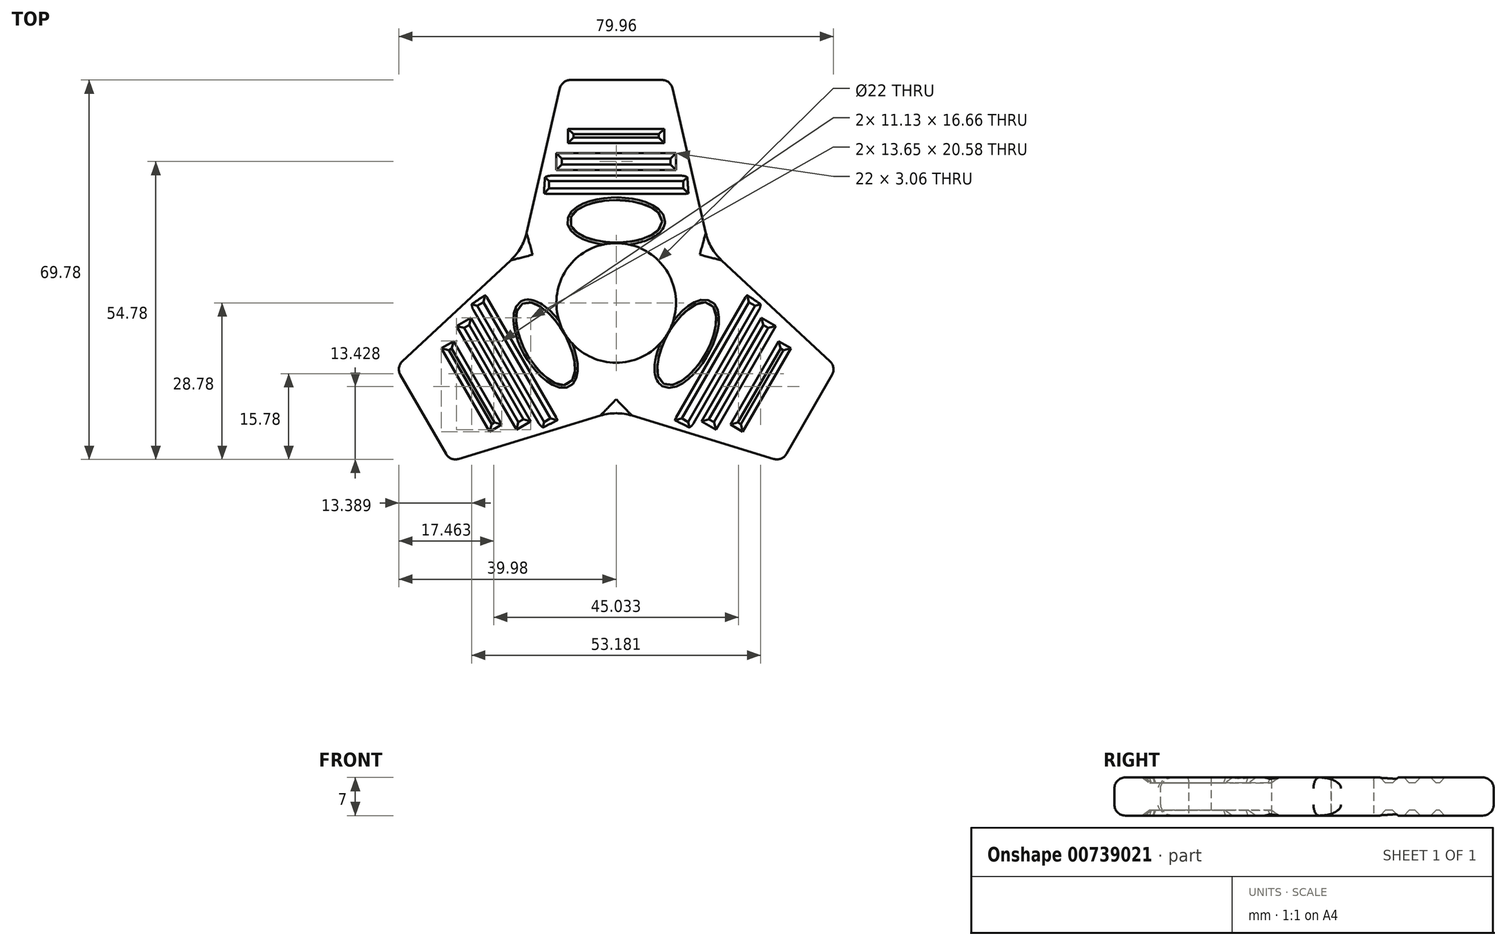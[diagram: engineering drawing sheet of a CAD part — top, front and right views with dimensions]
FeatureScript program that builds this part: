
annotation { "Feature Type Name" : "Feature", "Feature Type Description" : "" }
export const myFeature = defineFeature(function(context is Context, id is Id, definition is map)
    precondition{}
    {
        {
            var Q0;
            Q0=qCreatedBy(makeId("Top.planeOp"),FACE);
            var sketch = newSketch(context, id + "F0", { "sketchPlane" : qUnion([Q0])});
            skCircle(sketch, "E0", {"center": v(0, 0) * mm, "radius": 11 * mm});
            skLineSegment(sketch, "E1", {"start": v(0, 11) * mm, "end": v(0, 41) * mm});
            skLineSegment(sketch, "E2", {"start": v(0, 41) * mm, "end": v(10, 41) * mm});
            skLineSegment(sketch, "E3", {"start": v(0, 41) * mm, "end": v(-10, 41) * mm});
            skLineSegment(sketch, "E4", {"start": v(-10, 41) * mm, "end": v(-19.47, 0) * mm});
            skLineSegment(sketch, "E5", {"start": v(10, 41) * mm, "end": v(19.47, 0) * mm});
            skLineSegment(sketch, "E6", {"start": v(-19.47, 0) * mm, "end": v(-11, 0) * mm});
            skLineSegment(sketch, "E7", {"start": v(19.47, 0) * mm, "end": v(11, 0) * mm});
            skLineSegment(sketch, "E8.bottom", {"start": v(8.86, 32.01) * mm, "end": v(-8.86, 32.01) * mm});
            skLineSegment(sketch, "E8.top", {"start": v(8.86, 29.4) * mm, "end": v(-8.86, 29.4) * mm});
            skLineSegment(sketch, "E8.left", {"start": v(8.86, 32.01) * mm, "end": v(8.86, 29.4) * mm});
            skLineSegment(sketch, "E8.right", {"start": v(-8.86, 32.01) * mm, "end": v(-8.86, 29.4) * mm});
            skPoint(sketch, "E8.middle", {"position": v(0, 30.7) * mm});
            skLineSegment(sketch, "E9.bottom", {"start": v(11, 27.53) * mm, "end": v(-11, 27.53) * mm});
            skLineSegment(sketch, "E9.top", {"start": v(11, 24.47) * mm, "end": v(-11, 24.47) * mm});
            skLineSegment(sketch, "E9.left", {"start": v(11, 27.53) * mm, "end": v(11, 24.47) * mm});
            skLineSegment(sketch, "E9.right", {"start": v(-11, 27.53) * mm, "end": v(-11, 24.47) * mm});
            skPoint(sketch, "E9.middle", {"position": v(0, 26) * mm});
            skLineSegment(sketch, "E10.bottom", {"start": v(13.34, 23.4) * mm, "end": v(-13.34, 23.4) * mm});
            skLineSegment(sketch, "E10.top", {"start": v(13.34, 20.09) * mm, "end": v(-13.34, 20.09) * mm});
            skLineSegment(sketch, "E10.left", {"start": v(13.34, 23.4) * mm, "end": v(13.34, 20.09) * mm});
            skLineSegment(sketch, "E10.right", {"start": v(-13.34, 23.4) * mm, "end": v(-13.34, 20.09) * mm});
            skPoint(sketch, "E10.middle", {"position": v(0, 21.74) * mm});
            skSolve(sketch);
        }
        {
            var Q0;
            {var subQ0=sQuery(id+"F0.wireOp",EDGE,"E1");Q0=makeQuery(id+"F0.imprint","IMPRINT",FACE,{"disambiguationData":[TD([[makeQuery(id+"F0.imprint","IMPRINT",EDGE,{"derivedFrom":subQ0}),-1.0]])]});}
            var Q1;
            {var subQ0=sQuery(id+"F0.wireOp",EDGE,"E1");Q1=makeQuery(id+"F0.imprint","IMPRINT",FACE,{"disambiguationData":[TD([[makeQuery(id+"F0.imprint","IMPRINT",EDGE,{"derivedFrom":subQ0}),1.0]])]});}
            extrude(context, id + "F1", {"entities" : qUnion([Q0, Q1]), "endBound" : BoundingType.SYMMETRIC, "depth" : 7 * mm, "offsetDistance" : 25 * mm});
        }
        {
            var Q0;
            {var subQ5=sQuery(id+"F0.wireOp",EDGE,"E8.right");Q0=makeQuery(id+"F0.imprint","IMPRINT",FACE,{"disambiguationData":[TD([[makeQuery(id+"F0.imprint","IMPRINT",EDGE,{"derivedFrom":subQ5}),1.0]])]});}
            var Q1;
            {var subQ5=sQuery(id+"F0.wireOp",EDGE,"E8.left");Q1=makeQuery(id+"F0.imprint","IMPRINT",FACE,{"disambiguationData":[TD([[makeQuery(id+"F0.imprint","IMPRINT",EDGE,{"derivedFrom":subQ5}),-1.0]])]});}
            var Q2;
            {var subQ5=sQuery(id+"F0.wireOp",EDGE,"E9.left");Q2=makeQuery(id+"F0.imprint","IMPRINT",FACE,{"disambiguationData":[TD([[makeQuery(id+"F0.imprint","IMPRINT",EDGE,{"derivedFrom":subQ5}),-1.0]])]});}
            var Q3;
            {var subQ5=sQuery(id+"F0.wireOp",EDGE,"E9.right");Q3=makeQuery(id+"F0.imprint","IMPRINT",FACE,{"disambiguationData":[TD([[makeQuery(id+"F0.imprint","IMPRINT",EDGE,{"derivedFrom":subQ5}),1.0]])]});}
            var Q4;
            {var subQ5=sQuery(id+"F0.wireOp",EDGE,"E10.right");Q4=makeQuery(id+"F0.imprint","IMPRINT",FACE,{"disambiguationData":[TD([[makeQuery(id+"F0.imprint","IMPRINT",EDGE,{"derivedFrom":subQ5}),1.0]])]});}
            var Q5;
            {var subQ5=sQuery(id+"F0.wireOp",EDGE,"E10.left");Q5=makeQuery(id+"F0.imprint","IMPRINT",FACE,{"disambiguationData":[TD([[makeQuery(id+"F0.imprint","IMPRINT",EDGE,{"derivedFrom":subQ5}),-1.0]])]});}
            extrude(context, id + "F2", {"entities" : qUnion([Q0, Q1, Q2, Q3, Q4, Q5]), "operationType" : NewBodyOperationType.ADD, "endBound" : BoundingType.SYMMETRIC, "depth" : 5 * mm, "offsetDistance" : 25 * mm});
        }
        {
            var Q0;
            Q0=makeQuery(id+"F2.opExtrude","CAP_EDGE",EDGE,{"disambiguationData":[OSD([sQuery(id+"F0.wireOp",EDGE,"E8.bottom")])],"isStart":false});
            var Q1;
            Q1=makeQuery(id+"F2.opExtrude","CAP_EDGE",EDGE,{"disambiguationData":[OSD([sQuery(id+"F0.wireOp",EDGE,"E8.left")])],"isStart":false});
            var Q2;
            Q2=makeQuery(id+"F2.opExtrude","CAP_FACE",FACE,{"disambiguationData":[OSD([sQuery(id+"F0.wireOp",EDGE,"E8.bottom"),sQuery(id+"F0.wireOp",EDGE,"E8.top"),sQuery(id+"F0.wireOp",EDGE,"E8.left"),sQuery(id+"F0.wireOp",EDGE,"E8.right")])],"isStart":false});
            var Q3;
            Q3=makeQuery(id+"F2.opExtrude","CAP_FACE",FACE,{"disambiguationData":[OSD([sQuery(id+"F0.wireOp",EDGE,"E9.bottom"),sQuery(id+"F0.wireOp",EDGE,"E9.top"),sQuery(id+"F0.wireOp",EDGE,"E9.left"),sQuery(id+"F0.wireOp",EDGE,"E9.right")])],"isStart":false});
            var Q4;
            Q4=makeQuery(id+"F2.opExtrude","CAP_FACE",FACE,{"disambiguationData":[OSD([sQuery(id+"F0.wireOp",EDGE,"E10.bottom"),sQuery(id+"F0.wireOp",EDGE,"E10.top"),sQuery(id+"F0.wireOp",EDGE,"E10.left"),sQuery(id+"F0.wireOp",EDGE,"E10.right")])],"isStart":false});
            chamfer(context, id + "F3", {"entities" : qUnion([Q0, Q1, Q2, Q3, Q4]), "chamferType" : ChamferType.OFFSET_ANGLE, "width" : 1 * mm, "oppositeDirection" : false, "angle" : 45 * degree, "tangentPropagation" : true});
        }
        {
            var Q0;
            Q0=makeQuery(id+"F2.opExtrude","CAP_FACE",FACE,{"disambiguationData":[OSD([sQuery(id+"F0.wireOp",EDGE,"E8.bottom"),sQuery(id+"F0.wireOp",EDGE,"E8.top"),sQuery(id+"F0.wireOp",EDGE,"E8.left"),sQuery(id+"F0.wireOp",EDGE,"E8.right")])],"isStart":true});
            var Q1;
            Q1=makeQuery(id+"F2.opExtrude","CAP_FACE",FACE,{"disambiguationData":[OSD([sQuery(id+"F0.wireOp",EDGE,"E9.bottom"),sQuery(id+"F0.wireOp",EDGE,"E9.top"),sQuery(id+"F0.wireOp",EDGE,"E9.left"),sQuery(id+"F0.wireOp",EDGE,"E9.right")])],"isStart":true});
            var Q2;
            Q2=makeQuery(id+"F2.opExtrude","CAP_FACE",FACE,{"disambiguationData":[OSD([sQuery(id+"F0.wireOp",EDGE,"E10.bottom"),sQuery(id+"F0.wireOp",EDGE,"E10.top"),sQuery(id+"F0.wireOp",EDGE,"E10.left"),sQuery(id+"F0.wireOp",EDGE,"E10.right")])],"isStart":true});
            chamfer(context, id + "F4", {"entities" : qUnion([Q0, Q1, Q2]), "chamferType" : ChamferType.OFFSET_ANGLE, "width" : 1 * mm, "oppositeDirection" : false, "angle" : 45 * degree, "tangentPropagation" : true});
        }
        {
            var Q0;
            Q0=makeQuery(id+"F1.opExtrude","CAP_EDGE",EDGE,{"disambiguationData":[OSD([sQuery(id+"F0.wireOp",EDGE,"E4")])],"isStart":false});
            var Q1;
            Q1=makeQuery(id+"F1.opExtrude","SWEPT_FACE",FACE,{"disambiguationData":[OSD([sQuery(id+"F0.wireOp",EDGE,"E2"),sQuery(id+"F0.wireOp",EDGE,"E3")])]});
            var Q2;
            Q2=makeQuery(id+"F1.opExtrude","CAP_EDGE",EDGE,{"disambiguationData":[OSD([sQuery(id+"F0.wireOp",EDGE,"E5")])],"isStart":false});
            var Q3;
            Q3=makeQuery(id+"F1.opExtrude","CAP_EDGE",EDGE,{"disambiguationData":[OSD([sQuery(id+"F0.wireOp",EDGE,"E5")])],"isStart":true});
            var Q4;
            Q4=makeQuery(id+"F1.opExtrude","CAP_EDGE",EDGE,{"disambiguationData":[OSD([sQuery(id+"F0.wireOp",EDGE,"E4")])],"isStart":true});
            fillet(context, id + "F5", {"entities" : qUnion([Q0, Q1, Q2, Q3, Q4]), "radius" : 2 * mm, "tangentPropagation" : true, "allowEdgeOverflow" : false});
        }
        {
            var Q0;
            Q0=makeQuery(id+"F1.opExtrude","SWEPT_BODY",BODY,{"disambiguationData":[OSD([sQuery(id+"F0.wireOp",EDGE,"E0"),sQuery(id+"F0.wireOp",EDGE,"E2"),sQuery(id+"F0.wireOp",EDGE,"E3"),sQuery(id+"F0.wireOp",EDGE,"E4"),sQuery(id+"F0.wireOp",EDGE,"E5"),sQuery(id+"F0.wireOp",EDGE,"E6"),sQuery(id+"F0.wireOp",EDGE,"E7")])]});
            var Q1;
            Q1=sQuery(id+"F0.wireOp",EDGE,"E0");
            circularPattern(context, id + "F6", {"operationType" : NewBodyOperationType.ADD, "entities" : qUnion([Q0]), "axis" : qUnion([Q1]), "angle" : 360 * degree, "instanceCount" : 3, "equalSpace" : true});
        }
        {
            var Q0;
            Q0=qCreatedBy(makeId("Top.planeOp"),FACE);
            var sketch = newSketch(context, id + "F7", { "sketchPlane" : qUnion([Q0])});
            skLineSegment(sketch, "E11", {"start": v(0, 0) * mm, "end": v(0, 15) * mm});
            skEllipse(sketch, "E12", {"center": v(0, 15) * mm, "majorRadius": 8.5 * mm, "minorRadius": 3.9 * mm, "majorAxis": v(1, 0)});
            skSolve(sketch);
        }
        {
            var Q0;
            Q0 = qSketchRegion(id + "F7", true);
            extrude(context, id + "F8", {"entities" : qUnion([Q0]), "endBound" : BoundingType.SYMMETRIC, "depth" : 8 * mm, "offsetDistance" : 25 * mm});
        }
        {
            var Q0;
            Q0=makeQuery(id+"F8.opExtrude","SWEPT_BODY",BODY,{"disambiguationData":[OSD([sQuery(id+"F7.wireOp",EDGE,"E12")])]});
            var Q1;
            {var subQ0=makeQuery(id+"F1.opExtrude","CAP_EDGE",EDGE,{"disambiguationData":[OSD([sQuery(id+"F0.wireOp",EDGE,"E0")])],"isStart":true});Q1=makeQuery(id+"F6.boolean.opBoolean","MERGE",EDGE,{"derivedFrom":[subQ0,makeQuery(id+"F6.opPattern","COPY",EDGE,{"derivedFrom":subQ0,"instanceName":"1"}),makeQuery(id+"F6.opPattern","COPY",EDGE,{"derivedFrom":subQ0,"instanceName":"2"})]});}
            circularPattern(context, id + "F9", {"operationType" : NewBodyOperationType.REMOVE, "entities" : qUnion([Q0]), "axis" : qUnion([Q1]), "angle" : 360 * degree, "instanceCount" : 3, "oppositeDirection" : true, "equalSpace" : true});
        }
        {
            var Q0;
            {var subQ0=makeQuery(id+"F09wqxZ7iDstZk3_1.opFillet","SPLIT",FACE,{"disambiguationData":[OD(0.0)],"derivedFrom":makeQuery(id+"F1.opExtrude","CAP_FACE",FACE,{"disambiguationData":[OSD([sQuery(id+"F0.wireOp",EDGE,"E0"),sQuery(id+"F0.wireOp",EDGE,"E2"),sQuery(id+"F0.wireOp",EDGE,"E3"),sQuery(id+"F0.wireOp",EDGE,"E4"),sQuery(id+"F0.wireOp",EDGE,"E5"),sQuery(id+"F0.wireOp",EDGE,"E6"),sQuery(id+"F0.wireOp",EDGE,"E7"),sQuery(id+"F0.wireOp",EDGE,"E8.bottom"),sQuery(id+"F0.wireOp",EDGE,"E8.top"),sQuery(id+"F0.wireOp",EDGE,"E8.left"),sQuery(id+"F0.wireOp",EDGE,"E8.right"),sQuery(id+"F0.wireOp",EDGE,"E9.bottom"),sQuery(id+"F0.wireOp",EDGE,"E9.top"),sQuery(id+"F0.wireOp",EDGE,"E9.left"),sQuery(id+"F0.wireOp",EDGE,"E9.right"),sQuery(id+"F0.wireOp",EDGE,"E10.bottom"),sQuery(id+"F0.wireOp",EDGE,"E10.top"),sQuery(id+"F0.wireOp",EDGE,"E10.left"),sQuery(id+"F0.wireOp",EDGE,"E10.right")])],"isStart":false})});Q0=makeQuery(id+"F9.boolean.opBoolean","INTERSECT",EDGE,{"derivedFrom":[makeQuery(id+"F6.boolean.opBoolean","MERGE",FACE,{"derivedFrom":[subQ0,makeQuery(id+"F6.opPattern","COPY",FACE,{"derivedFrom":subQ0,"instanceName":"1"}),makeQuery(id+"F6.opPattern","COPY",FACE,{"derivedFrom":subQ0,"instanceName":"2"})]}),makeQuery(id+"F8.opExtrude","SWEPT_FACE",FACE,{"disambiguationData":[OSD([sQuery(id+"F7.wireOp",EDGE,"E12")])]})]});}
            var Q1;
            Q1=makeQuery(id+"F9.boolean.opBoolean","COPY",EDGE,{"derivedFrom":makeQuery(id+"F8.opExtrude","CAP_EDGE",EDGE,{"disambiguationData":[OSD([sQuery(id+"F7.wireOp",EDGE,"E12")])],"isStart":true})});
            var Q2;
            {var subQ0=makeQuery(id+"F09wqxZ7iDstZk3_1.opFillet","SPLIT",FACE,{"disambiguationData":[OD(0.0)],"derivedFrom":makeQuery(id+"F1.opExtrude","CAP_FACE",FACE,{"disambiguationData":[OSD([sQuery(id+"F0.wireOp",EDGE,"E0"),sQuery(id+"F0.wireOp",EDGE,"E2"),sQuery(id+"F0.wireOp",EDGE,"E3"),sQuery(id+"F0.wireOp",EDGE,"E4"),sQuery(id+"F0.wireOp",EDGE,"E5"),sQuery(id+"F0.wireOp",EDGE,"E6"),sQuery(id+"F0.wireOp",EDGE,"E7"),sQuery(id+"F0.wireOp",EDGE,"E8.bottom"),sQuery(id+"F0.wireOp",EDGE,"E8.top"),sQuery(id+"F0.wireOp",EDGE,"E8.left"),sQuery(id+"F0.wireOp",EDGE,"E8.right"),sQuery(id+"F0.wireOp",EDGE,"E9.bottom"),sQuery(id+"F0.wireOp",EDGE,"E9.top"),sQuery(id+"F0.wireOp",EDGE,"E9.left"),sQuery(id+"F0.wireOp",EDGE,"E9.right"),sQuery(id+"F0.wireOp",EDGE,"E10.bottom"),sQuery(id+"F0.wireOp",EDGE,"E10.top"),sQuery(id+"F0.wireOp",EDGE,"E10.left"),sQuery(id+"F0.wireOp",EDGE,"E10.right")])],"isStart":false})});Q2=makeQuery(id+"F9.boolean.opBoolean","INTERSECT",EDGE,{"derivedFrom":[makeQuery(id+"F6.boolean.opBoolean","MERGE",FACE,{"derivedFrom":[subQ0,makeQuery(id+"F6.opPattern","COPY",FACE,{"derivedFrom":subQ0,"instanceName":"1"}),makeQuery(id+"F6.opPattern","COPY",FACE,{"derivedFrom":subQ0,"instanceName":"2"})]}),makeQuery(id+"F9.opPattern","COPY",FACE,{"derivedFrom":makeQuery(id+"F8.opExtrude","SWEPT_FACE",FACE,{"disambiguationData":[OSD([sQuery(id+"F7.wireOp",EDGE,"E12")])]}),"instanceName":"2"})]});}
            var Q3;
            Q3=makeQuery(id+"F9.boolean.opBoolean","COPY",EDGE,{"derivedFrom":makeQuery(id+"F9.opPattern","COPY",EDGE,{"derivedFrom":makeQuery(id+"F8.opExtrude","CAP_EDGE",EDGE,{"disambiguationData":[OSD([sQuery(id+"F7.wireOp",EDGE,"E12")])],"isStart":true}),"instanceName":"2"})});
            var Q4;
            {var subQ0=makeQuery(id+"F09wqxZ7iDstZk3_1.opFillet","SPLIT",FACE,{"disambiguationData":[OD(0.0)],"derivedFrom":makeQuery(id+"F1.opExtrude","CAP_FACE",FACE,{"disambiguationData":[OSD([sQuery(id+"F0.wireOp",EDGE,"E0"),sQuery(id+"F0.wireOp",EDGE,"E2"),sQuery(id+"F0.wireOp",EDGE,"E3"),sQuery(id+"F0.wireOp",EDGE,"E4"),sQuery(id+"F0.wireOp",EDGE,"E5"),sQuery(id+"F0.wireOp",EDGE,"E6"),sQuery(id+"F0.wireOp",EDGE,"E7"),sQuery(id+"F0.wireOp",EDGE,"E8.bottom"),sQuery(id+"F0.wireOp",EDGE,"E8.top"),sQuery(id+"F0.wireOp",EDGE,"E8.left"),sQuery(id+"F0.wireOp",EDGE,"E8.right"),sQuery(id+"F0.wireOp",EDGE,"E9.bottom"),sQuery(id+"F0.wireOp",EDGE,"E9.top"),sQuery(id+"F0.wireOp",EDGE,"E9.left"),sQuery(id+"F0.wireOp",EDGE,"E9.right"),sQuery(id+"F0.wireOp",EDGE,"E10.bottom"),sQuery(id+"F0.wireOp",EDGE,"E10.top"),sQuery(id+"F0.wireOp",EDGE,"E10.left"),sQuery(id+"F0.wireOp",EDGE,"E10.right")])],"isStart":false})});Q4=makeQuery(id+"F9.boolean.opBoolean","INTERSECT",EDGE,{"derivedFrom":[makeQuery(id+"F6.boolean.opBoolean","MERGE",FACE,{"derivedFrom":[subQ0,makeQuery(id+"F6.opPattern","COPY",FACE,{"derivedFrom":subQ0,"instanceName":"1"}),makeQuery(id+"F6.opPattern","COPY",FACE,{"derivedFrom":subQ0,"instanceName":"2"})]}),makeQuery(id+"F9.opPattern","COPY",FACE,{"derivedFrom":makeQuery(id+"F8.opExtrude","SWEPT_FACE",FACE,{"disambiguationData":[OSD([sQuery(id+"F7.wireOp",EDGE,"E12")])]}),"instanceName":"1"})]});}
            var Q5;
            Q5=makeQuery(id+"F9.boolean.opBoolean","COPY",EDGE,{"derivedFrom":makeQuery(id+"F9.opPattern","COPY",EDGE,{"derivedFrom":makeQuery(id+"F8.opExtrude","CAP_EDGE",EDGE,{"disambiguationData":[OSD([sQuery(id+"F7.wireOp",EDGE,"E12")])],"isStart":true}),"instanceName":"1"})});
            fillet(context, id + "F10", {"entities" : qUnion([Q0, Q1, Q2, Q3, Q4, Q5]), "radius" : .5 * mm, "tangentPropagation" : true, "allowEdgeOverflow" : false});
        }
        {
            var Q0;
            {var subQ0=sQuery(id+"F0.wireOp",EDGE,"E4");var subQ1=sQuery(id+"F0.wireOp",EDGE,"E5");Q0=makeQuery(id+"F6.boolean.opBoolean","INTERSECT",EDGE,{"derivedFrom":[makeQuery(id+"F5.opFillet","BLEND_FACE",FACE,{"disambiguationData":[OSD([subQ1]),TDD([makeQuery(id+"F1.opExtrude","CAP_EDGE",EDGE,{"disambiguationData":[OSD([subQ1])],"isStart":false})])]}),makeQuery(id+"F6.opPattern","COPY",FACE,{"derivedFrom":makeQuery(id+"F5.opFillet","BLEND_FACE",FACE,{"disambiguationData":[OSD([subQ0]),TDD([makeQuery(id+"F1.opExtrude","CAP_EDGE",EDGE,{"disambiguationData":[OSD([subQ0])],"isStart":false})])]}),"instanceName":"2"})]});}
            var Q1;
            Q1=makeQuery(id+"F6.boolean.opBoolean","INTERSECT",EDGE,{"derivedFrom":[makeQuery(id+"F1.opExtrude","SWEPT_FACE",FACE,{"disambiguationData":[OSD([sQuery(id+"F0.wireOp",EDGE,"E5")])]}),makeQuery(id+"F6.opPattern","COPY",FACE,{"derivedFrom":makeQuery(id+"F1.opExtrude","SWEPT_FACE",FACE,{"disambiguationData":[OSD([sQuery(id+"F0.wireOp",EDGE,"E4")])]}),"instanceName":"2"})]});
            var Q2;
            {var subQ0=sQuery(id+"F0.wireOp",EDGE,"E4");var subQ1=sQuery(id+"F0.wireOp",EDGE,"E5");Q2=makeQuery(id+"F6.boolean.opBoolean","INTERSECT",EDGE,{"derivedFrom":[makeQuery(id+"F5.opFillet","BLEND_FACE",FACE,{"disambiguationData":[OSD([subQ1]),TDD([makeQuery(id+"F1.opExtrude","CAP_EDGE",EDGE,{"disambiguationData":[OSD([subQ1])],"isStart":true})])]}),makeQuery(id+"F6.opPattern","COPY",FACE,{"derivedFrom":makeQuery(id+"F5.opFillet","BLEND_FACE",FACE,{"disambiguationData":[OSD([subQ0]),TDD([makeQuery(id+"F1.opExtrude","CAP_EDGE",EDGE,{"disambiguationData":[OSD([subQ0])],"isStart":true})])]}),"instanceName":"2"})]});}
            var Q3;
            Q3=makeQuery(id+"F6.boolean.opBoolean","INTERSECT",EDGE,{"derivedFrom":[makeQuery(id+"F6.opPattern","COPY",FACE,{"derivedFrom":makeQuery(id+"F1.opExtrude","SWEPT_FACE",FACE,{"disambiguationData":[OSD([sQuery(id+"F0.wireOp",EDGE,"E4")])]}),"instanceName":"1"}),makeQuery(id+"F6.opPattern","COPY",FACE,{"derivedFrom":makeQuery(id+"F1.opExtrude","SWEPT_FACE",FACE,{"disambiguationData":[OSD([sQuery(id+"F0.wireOp",EDGE,"E5")])]}),"instanceName":"2"})]});
            var Q4;
            {var subQ0=sQuery(id+"F0.wireOp",EDGE,"E5");var subQ1=sQuery(id+"F0.wireOp",EDGE,"E4");Q4=makeQuery(id+"F6.boolean.opBoolean","INTERSECT",EDGE,{"derivedFrom":[makeQuery(id+"F6.opPattern","COPY",FACE,{"derivedFrom":makeQuery(id+"F5.opFillet","BLEND_FACE",FACE,{"disambiguationData":[OSD([subQ1]),TDD([makeQuery(id+"F1.opExtrude","CAP_EDGE",EDGE,{"disambiguationData":[OSD([subQ1])],"isStart":false})])]}),"instanceName":"1"}),makeQuery(id+"F6.opPattern","COPY",FACE,{"derivedFrom":makeQuery(id+"F5.opFillet","BLEND_FACE",FACE,{"disambiguationData":[OSD([subQ0]),TDD([makeQuery(id+"F1.opExtrude","CAP_EDGE",EDGE,{"disambiguationData":[OSD([subQ0])],"isStart":false})])]}),"instanceName":"2"})]});}
            var Q5;
            {var subQ0=sQuery(id+"F0.wireOp",EDGE,"E5");var subQ1=sQuery(id+"F0.wireOp",EDGE,"E4");Q5=makeQuery(id+"F6.boolean.opBoolean","INTERSECT",EDGE,{"derivedFrom":[makeQuery(id+"F6.opPattern","COPY",FACE,{"derivedFrom":makeQuery(id+"F5.opFillet","BLEND_FACE",FACE,{"disambiguationData":[OSD([subQ1]),TDD([makeQuery(id+"F1.opExtrude","CAP_EDGE",EDGE,{"disambiguationData":[OSD([subQ1])],"isStart":true})])]}),"instanceName":"1"}),makeQuery(id+"F6.opPattern","COPY",FACE,{"derivedFrom":makeQuery(id+"F5.opFillet","BLEND_FACE",FACE,{"disambiguationData":[OSD([subQ0]),TDD([makeQuery(id+"F1.opExtrude","CAP_EDGE",EDGE,{"disambiguationData":[OSD([subQ0])],"isStart":true})])]}),"instanceName":"2"})]});}
            var Q6;
            Q6=makeQuery(id+"F6.boolean.opBoolean","INTERSECT",EDGE,{"derivedFrom":[makeQuery(id+"F1.opExtrude","SWEPT_FACE",FACE,{"disambiguationData":[OSD([sQuery(id+"F0.wireOp",EDGE,"E4")])]}),makeQuery(id+"F6.opPattern","COPY",FACE,{"derivedFrom":makeQuery(id+"F1.opExtrude","SWEPT_FACE",FACE,{"disambiguationData":[OSD([sQuery(id+"F0.wireOp",EDGE,"E5")])]}),"instanceName":"1"})]});
            fillet(context, id + "F11", {"entities" : qUnion([Q0, Q1, Q2, Q3, Q4, Q5, Q6]), "radius" : 10 * mm, "tangentPropagation" : true, "allowEdgeOverflow" : false});
        }
    });
